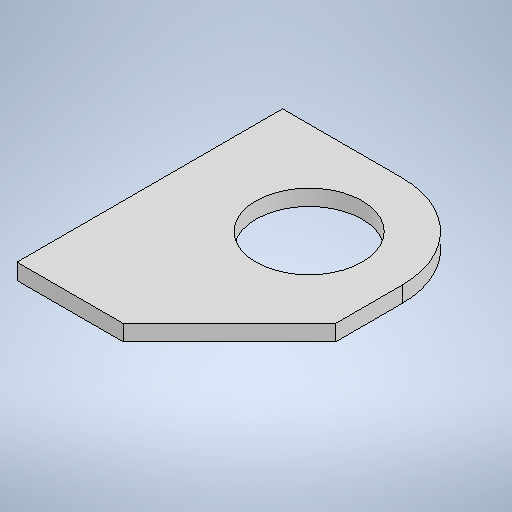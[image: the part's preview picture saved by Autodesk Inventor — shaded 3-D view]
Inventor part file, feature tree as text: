
AUTODESK INVENTOR PART (.ipt)
format: ipt  version: 2025 (Build 290162010, 162A)  size: 272,896 bytes
history: native  units: mm
features: other x2, sheet_metal_op x1, sketch x1
ambient origin geometry x8: Origin, YZ Plane, XZ Plane, XY Plane, X Axis, Y Axis, Z Axis, Center Point
bodies: Body1 (feature_tree)
feature tree (4):
  sheet_metal_op  "Face2"
  sketch  "Sketch6"  dims[d41=80.0mm d42=15.0mm d43=40.0mm d44=35.0mm d45=45.0mm d46=6.0mm d47=20.0mm d48=135.0deg d49=40.0mm]
  other  "Plate3"
  other  "Definition1"
